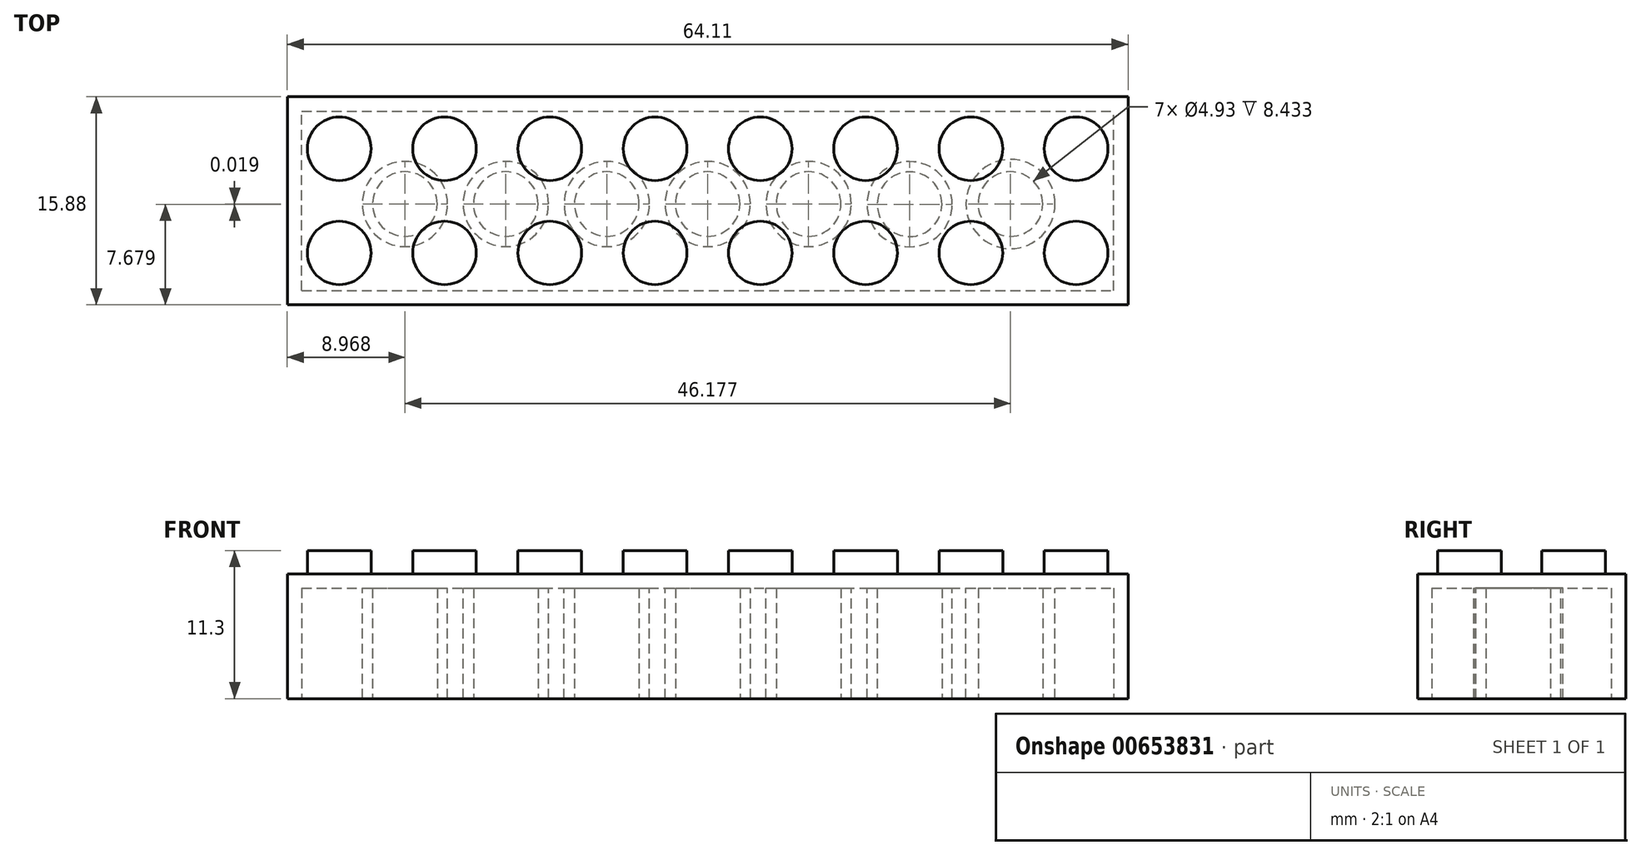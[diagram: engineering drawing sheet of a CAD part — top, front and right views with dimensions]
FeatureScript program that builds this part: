
annotation { "Feature Type Name" : "Feature", "Feature Type Description" : "" }
export const myFeature = defineFeature(function(context is Context, id is Id, definition is map)
    precondition{}
    {
        {
            var Q0;
            Q0=qCreatedBy(makeId("Top.planeOp"),FACE);
            var sketch = newSketch(context, id + "F0", { "sketchPlane" : qUnion([Q0])});
            skLineSegment(sketch, "E0.bottom", {"start": v(-39.42, 22.76) * mm, "end": v(24.7, 22.76) * mm});
            skLineSegment(sketch, "E0.top", {"start": v(-39.42, 6.88) * mm, "end": v(24.7, 6.88) * mm});
            skLineSegment(sketch, "E0.left", {"start": v(-39.42, 22.76) * mm, "end": v(-39.42, 6.88) * mm});
            skLineSegment(sketch, "E0.right", {"start": v(24.7, 22.76) * mm, "end": v(24.7, 6.88) * mm});
            skSolve(sketch);
        }
        {
            var Q0;
            Q0 = qSketchRegion(id + "F0", true);
            extrude(context, id + "F1", {"entities" : qUnion([Q0]), "depth" : 9.52 * mm, "offsetDistance" : 25.4 * mm});
        }
        {
            var Q0;
            Q0=makeQuery(id+"F1.opExtrude","CAP_FACE",FACE,{"disambiguationData":[OSD([sQuery(id+"F0.wireOp",EDGE,"E0.bottom"),sQuery(id+"F0.wireOp",EDGE,"E0.top"),sQuery(id+"F0.wireOp",EDGE,"E0.left"),sQuery(id+"F0.wireOp",EDGE,"E0.right")])],"isStart":false});
            var sketch = newSketch(context, id + "F2", { "sketchPlane" : qUnion([Q0])});
            skCircle(sketch, "E1", {"center": v(-35.46, 18.8) * mm, "radius": 2.43 * mm});
            skCircle(sketch, "E2", {"center": v(-27.43, 18.8) * mm, "radius": 2.43 * mm});
            skCircle(sketch, "E3", {"center": v(-19.4, 18.8) * mm, "radius": 2.43 * mm});
            skCircle(sketch, "E4", {"center": v(-11.38, 18.8) * mm, "radius": 2.43 * mm});
            skCircle(sketch, "E5", {"center": v(-3.35, 18.8) * mm, "radius": 2.43 * mm});
            skCircle(sketch, "E6", {"center": v(4.68, 18.8) * mm, "radius": 2.43 * mm});
            skCircle(sketch, "E7", {"center": v(12.7, 18.8) * mm, "radius": 2.43 * mm});
            skCircle(sketch, "E8", {"center": v(20.73, 18.8) * mm, "radius": 2.43 * mm});
            skCircle(sketch, "E9", {"center": v(-35.46, 10.84) * mm, "radius": 2.43 * mm});
            skCircle(sketch, "E10", {"center": v(-27.43, 10.84) * mm, "radius": 2.43 * mm});
            skCircle(sketch, "E11", {"center": v(-19.4, 10.84) * mm, "radius": 2.43 * mm});
            skCircle(sketch, "E12", {"center": v(-11.38, 10.84) * mm, "radius": 2.43 * mm});
            skCircle(sketch, "E13", {"center": v(-3.35, 10.84) * mm, "radius": 2.43 * mm});
            skCircle(sketch, "E14", {"center": v(4.68, 10.84) * mm, "radius": 2.43 * mm});
            skCircle(sketch, "E15", {"center": v(20.73, 10.84) * mm, "radius": 2.43 * mm});
            skCircle(sketch, "E16", {"center": v(12.7, 10.84) * mm, "radius": 2.43 * mm});
            skSolve(sketch);
        }
        {
            var Q0;
            Q0 = qSketchRegion(id + "F2", true);
            extrude(context, id + "F3", {"entities" : qUnion([Q0]), "operationType" : NewBodyOperationType.ADD, "depth" : 1.78 * mm, "offsetDistance" : 25.4 * mm});
        }
        {
            var Q0;
            Q0=makeQuery(id+"F1.opExtrude","CAP_FACE",FACE,{"disambiguationData":[OSD([sQuery(id+"F0.wireOp",EDGE,"E0.bottom"),sQuery(id+"F0.wireOp",EDGE,"E0.top"),sQuery(id+"F0.wireOp",EDGE,"E0.left"),sQuery(id+"F0.wireOp",EDGE,"E0.right")])],"isStart":true});
            var sketch = newSketch(context, id + "F4", { "sketchPlane" : qUnion([Q0])});
            skLineSegment(sketch, "E17.bottom", {"start": v(-38.33, -7.97) * mm, "end": v(23.6, -7.97) * mm});
            skLineSegment(sketch, "E17.top", {"start": v(-38.33, -21.66) * mm, "end": v(23.6, -21.66) * mm});
            skLineSegment(sketch, "E17.left", {"start": v(-38.33, -7.97) * mm, "end": v(-38.33, -21.66) * mm});
            skLineSegment(sketch, "E17.right", {"start": v(23.6, -7.97) * mm, "end": v(23.6, -21.66) * mm});
            skSolve(sketch);
        }
        {
            var Q0;
            Q0 = qSketchRegion(id + "F4", true);
            extrude(context, id + "F5", {"entities" : qUnion([Q0]), "operationType" : NewBodyOperationType.REMOVE, "oppositeDirection" : true, "depth" : 8.43 * mm, "offsetDistance" : 25.4 * mm});
        }
        {
            var Q0;
            Q0=makeQuery(id+"F5.boolean.opBoolean","COPY",FACE,{"derivedFrom":makeQuery(id+"F5.opExtrude","CAP_FACE",FACE,{"disambiguationData":[OSD([sQuery(id+"F4.wireOp",EDGE,"E17.bottom"),sQuery(id+"F4.wireOp",EDGE,"E17.top"),sQuery(id+"F4.wireOp",EDGE,"E17.left"),sQuery(id+"F4.wireOp",EDGE,"E17.right")])],"isStart":false})});
            var sketch = newSketch(context, id + "F6", { "sketchPlane" : qUnion([Q0])});
            skCircle(sketch, "E18", {"center": v(-30.45, -14.58) * mm, "radius": 3.25 * mm});
            skCircle(sketch, "E19", {"center": v(15.72, -14.58) * mm, "radius": 3.4 * mm});
            skCircle(sketch, "E20", {"center": v(-22.76, -14.58) * mm, "radius": 3.25 * mm});
            skCircle(sketch, "E21", {"center": v(-15.06, -14.58) * mm, "radius": 3.25 * mm});
            skCircle(sketch, "E22", {"center": v(-7.36, -14.58) * mm, "radius": 3.25 * mm});
            skCircle(sketch, "E23", {"center": v(0.33, -14.58) * mm, "radius": 3.25 * mm});
            skCircle(sketch, "E24", {"center": v(8.03, -14.56) * mm, "radius": 3.25 * mm});
            skSolve(sketch);
        }
        {
            var Q0;
            Q0 = qSketchRegion(id + "F6", true);
            extrude(context, id + "F7", {"entities" : qUnion([Q0]), "operationType" : NewBodyOperationType.ADD, "depth" : 8.43 * mm, "offsetDistance" : 25.4 * mm});
        }
        {
            var Q0;
            Q0=makeQuery(id+"F7.opExtrude","CAP_FACE",FACE,{"disambiguationData":[OSD([sQuery(id+"F6.wireOp",EDGE,"E18")])],"isStart":false});
            var sketch = newSketch(context, id + "F8", { "sketchPlane" : qUnion([Q0])});
            skCircle(sketch, "E25", {"center": v(-30.45, -14.58) * mm, "radius": 2.46 * mm});
            skCircle(sketch, "E26", {"center": v(-22.76, -14.58) * mm, "radius": 2.46 * mm});
            skCircle(sketch, "E27", {"center": v(-15.06, -14.58) * mm, "radius": 2.46 * mm});
            skCircle(sketch, "E28", {"center": v(-7.36, -14.58) * mm, "radius": 2.46 * mm});
            skCircle(sketch, "E29", {"center": v(0.33, -14.58) * mm, "radius": 2.46 * mm});
            skCircle(sketch, "E30", {"center": v(8.03, -14.56) * mm, "radius": 2.46 * mm});
            skCircle(sketch, "E31", {"center": v(15.72, -14.58) * mm, "radius": 2.46 * mm});
            skSolve(sketch);
        }
        {
            var Q0;
            Q0 = qSketchRegion(id + "F8", true);
            extrude(context, id + "F9", {"entities" : qUnion([Q0]), "operationType" : NewBodyOperationType.REMOVE, "oppositeDirection" : true, "depth" : 8.43 * mm, "offsetDistance" : 25.4 * mm});
        }
    });
